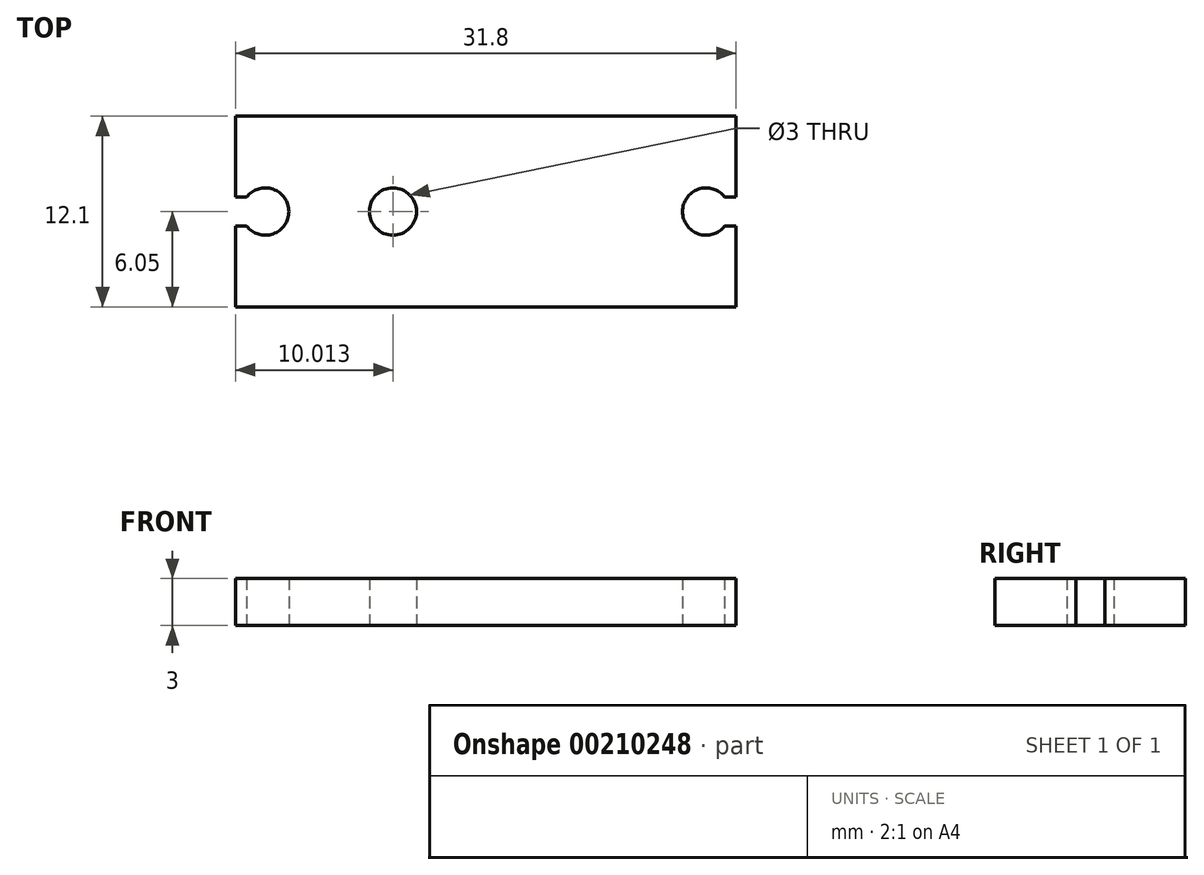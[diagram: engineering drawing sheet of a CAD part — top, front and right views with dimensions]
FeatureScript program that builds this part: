
annotation { "Feature Type Name" : "Feature", "Feature Type Description" : "" }
export const myFeature = defineFeature(function(context is Context, id is Id, definition is map)
    precondition{}
    {
        {
            var Q0;
            Q0=qCreatedBy(makeId("Top.planeOp"),FACE);
            var sketch = newSketch(context, id + "F0", { "sketchPlane" : qUnion([Q0])});
            skLineSegment(sketch, "E0.bottom", {"start": v(-15.9, 6.05) * mm, "end": v(15.9, 6.05) * mm});
            skLineSegment(sketch, "E0.top", {"start": v(-15.9, -6.05) * mm, "end": v(15.9, -6.05) * mm});
            skLineSegment(sketch, "E0.left", {"start": v(-15.9, 6.05) * mm, "end": v(-15.9, 0.93) * mm});
            skLineSegment(sketch, "E0.right", {"start": v(15.9, 6.05) * mm, "end": v(15.9, 0.93) * mm});
            skPoint(sketch, "E1", {"position": v(14, 0) * mm});
            skArc(sketch, "E2", {"start": v(15.18, 0.93) * mm, "mid": v(12.5, 0) * mm, "end": v(15.18, -0.93) * mm});
            skArc(sketch, "E3.MirrorC", {"start": v(-15.18, 0.93) * mm, "mid": v(-12.5, 0) * mm, "end": v(-15.18, -0.93) * mm});
            skPoint(sketch, "E4", {"position": v(-5.89, 0) * mm});
            skCircle(sketch, "E5", {"center": v(-5.89, 0) * mm, "radius": 1.5 * mm});
            skLineSegment(sketch, "E6", {"start": v(15.9, 0.93) * mm, "end": v(15.18, 0.93) * mm});
            skLineSegment(sketch, "E7.MirrorCS", {"start": v(15.9, -0.93) * mm, "end": v(15.18, -0.93) * mm});
            skPoint(sketch, "E8.orphan", {"position": v(14.9, 0.93) * mm});
            skPoint(sketch, "E9.orphan", {"position": v(14.9, -0.93) * mm});
            skLineSegment(sketch, "E10.MirrorCS", {"start": v(-15.9, -0.93) * mm, "end": v(-15.18, -0.93) * mm});
            skLineSegment(sketch, "E11.MirrorCS", {"start": v(-15.9, 0.93) * mm, "end": v(-15.18, 0.93) * mm});
            skLineSegment(sketch, "E12.trimOffspring", {"start": v(-15.9, -0.93) * mm, "end": v(-15.9, -6.05) * mm});
            skLineSegment(sketch, "E13.trimOffspring", {"start": v(15.9, -0.93) * mm, "end": v(15.9, -6.05) * mm});
            skSolve(sketch);
        }
        {
            var Q0;
            Q0 = qSketchRegion(id + "F0", true);
            extrude(context, id + "F1", {"entities" : qUnion([Q0]), "depth" : 3 * mm});
        }
    });
